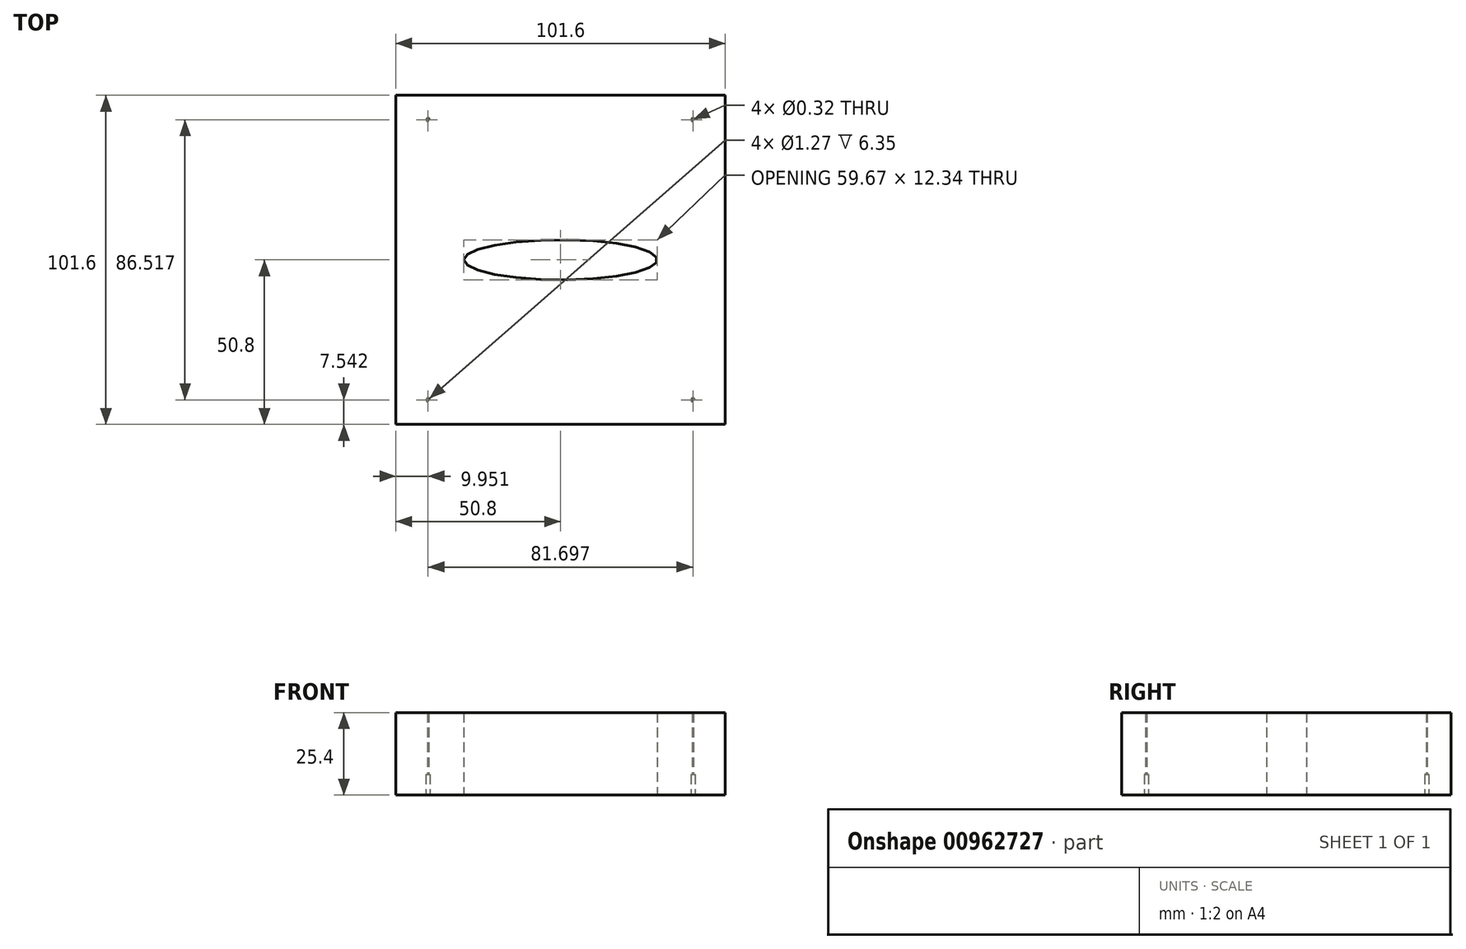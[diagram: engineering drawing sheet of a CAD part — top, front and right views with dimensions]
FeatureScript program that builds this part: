
annotation { "Feature Type Name" : "Feature", "Feature Type Description" : "" }
export const myFeature = defineFeature(function(context is Context, id is Id, definition is map)
    precondition{}
    {
        {
            var Q0;
            Q0=qCreatedBy(makeId("Top.planeOp"),FACE);
            var sketch = newSketch(context, id + "F0", { "sketchPlane" : qUnion([Q0])});
            skLineSegment(sketch, "E0.bottom", {"start": v(50.8, -50.8) * mm, "end": v(-50.8, -50.8) * mm});
            skLineSegment(sketch, "E0.top", {"start": v(50.8, 50.8) * mm, "end": v(-50.8, 50.8) * mm});
            skLineSegment(sketch, "E0.left", {"start": v(50.8, -50.8) * mm, "end": v(50.8, 50.8) * mm});
            skLineSegment(sketch, "E0.right", {"start": v(-50.8, -50.8) * mm, "end": v(-50.8, 50.8) * mm});
            skPoint(sketch, "E0.middle", {"position": v(0, 0) * mm});
            skEllipse(sketch, "E1", {"center": v(0, 0) * mm, "majorRadius": 29.83 * mm, "minorRadius": 6.17 * mm, "majorAxis": v(-1, 0)});
            skSolve(sketch);
        }
        {
            var Q0;
            Q0=makeQuery(id+"F0.imprint","IMPRINT",FACE,{"disambiguationData":[TD([[makeQuery(id+"F0.imprint","IMPRINT",EDGE,{"derivedFrom":sQuery(id+"F0.wireOp",EDGE,"E0.bottom")}),-1.0]])]});
            extrude(context, id + "F1", {"entities" : qUnion([Q0]), "depth" : 25.4 * mm, "offsetDistance" : 25.4 * mm});
        }
        {
            var Q0;
            Q0=makeQuery(id+"F1.opExtrude","CAP_FACE",FACE,{"disambiguationData":[OSD([sQuery(id+"F0.wireOp",EDGE,"E0.bottom"),sQuery(id+"F0.wireOp",EDGE,"E0.top"),sQuery(id+"F0.wireOp",EDGE,"E0.left"),sQuery(id+"F0.wireOp",EDGE,"E0.right"),sQuery(id+"F0.wireOp",EDGE,"E1")])],"isStart":true});
            var sketch = newSketch(context, id + "F2", { "sketchPlane" : qUnion([Q0])});
            skPoint(sketch, "E2", {"position": v(0, 50.8) * mm});
            skPoint(sketch, "E3", {"position": v(-40.85, 43.26) * mm});
            skPoint(sketch, "E4", {"position": v(40.85, 43.26) * mm});
            skPoint(sketch, "E5", {"position": v(-40.85, -43.26) * mm});
            skPoint(sketch, "E6", {"position": v(40.85, -43.26) * mm});
            skSolve(sketch);
        }
        {
            var Q0;
            Q0=sQuery(id+"F2.wireOp",VERTEX,"E3");
            var Q1;
            Q1=sQuery(id+"F2.wireOp",VERTEX,"E4");
            var Q2;
            Q2=sQuery(id+"F2.wireOp",VERTEX,"E6");
            var Q3;
            Q3=sQuery(id+"F2.wireOp",VERTEX,"E5");
            var Q4;
            Q4=makeQuery(id+"F1.opExtrude","SWEPT_BODY",BODY,{"disambiguationData":[OSD([sQuery(id+"F0.wireOp",EDGE,"E0.bottom"),sQuery(id+"F0.wireOp",EDGE,"E0.top"),sQuery(id+"F0.wireOp",EDGE,"E0.left"),sQuery(id+"F0.wireOp",EDGE,"E0.right"),sQuery(id+"F0.wireOp",EDGE,"E1")])]});
            hole(context, id + "F3", {"style" : HoleStyle.C_BORE, "endStyle" : HoleEndStyle.THROUGH, "holeDiameter" : 0.32 * mm, "cBoreDiameter" : 1.27 * mm, "cBoreDepth" : 6.35 * mm, "majorDiameter" : 6.35 * mm, "isTappedThrough" : true, "tappedDepth" : 12.7 * mm, "tapClearance" : 3, "locations" : qUnion([Q0, Q1, Q2, Q3]), "scope" : qUnion([Q4])});
        }
    });
